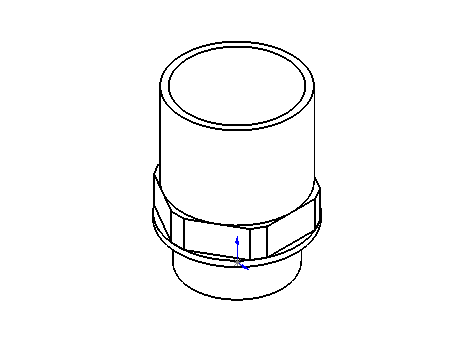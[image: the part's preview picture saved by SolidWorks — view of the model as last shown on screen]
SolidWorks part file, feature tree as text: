
SOLIDWORKS PART (.sldprt)
format: sldprt  version: not decoded by parser v0  size: 125,440 bytes
history: native  units: mm
features: sketch x6, extrude x4, plane x3, cut_extrude x2, material x1 (+8 scaffold rows collapsed)
feature tree (24):
  scaffold x8  (default folders/planes/origin — collapsed)
  material  "Material <not specified>"
  plane  "PRT Front"
  plane  "PRT Top"
  plane  "PRT Side"
  sketch  "Sketch2"  dims[D1=41.656mm]
  extrude  "Base-Extrude"  Depth=17.78mm
  sketch  "Sketch3"  dims[D1=54.9402mm]
  extrude  "Boss-Extrude1"  Depth=2.54mm
  sketch  "Sketch5"  dims[c1.D1=50.292mm c1.D2=~9.791423mm c2.D2=60.0deg c2.D3=~23.445512mm c3.D3=1.98deg c3.D4=~11.055177mm c4.D4=60.0deg c4.D5=50.292mm c4.D3=50.292mm]
  extrude  "Boss-Extrude3"  Depth=12.446mm
  sketch  "Sketch6"
  extrude  "Boss-Extrude4"  Depth=38.1mm
  sketch  "Sketch7"  dims[D1=44.704mm]
  cut_extrude  "Cut-Extrude1"  Depth=50.546mm
  sketch  "Sketch8"  dims[D1=34.29mm]
  cut_extrude  "Cut-Extrude2"  [1 undecoded]
decode coverage: 10 of 12 modeling features carry decoded parameters
note: ~ marks probable driven/reference dimensions
note: 1 parameter value undecoded
note: suppression state not decoded; provenance and decode notes live in map.json
